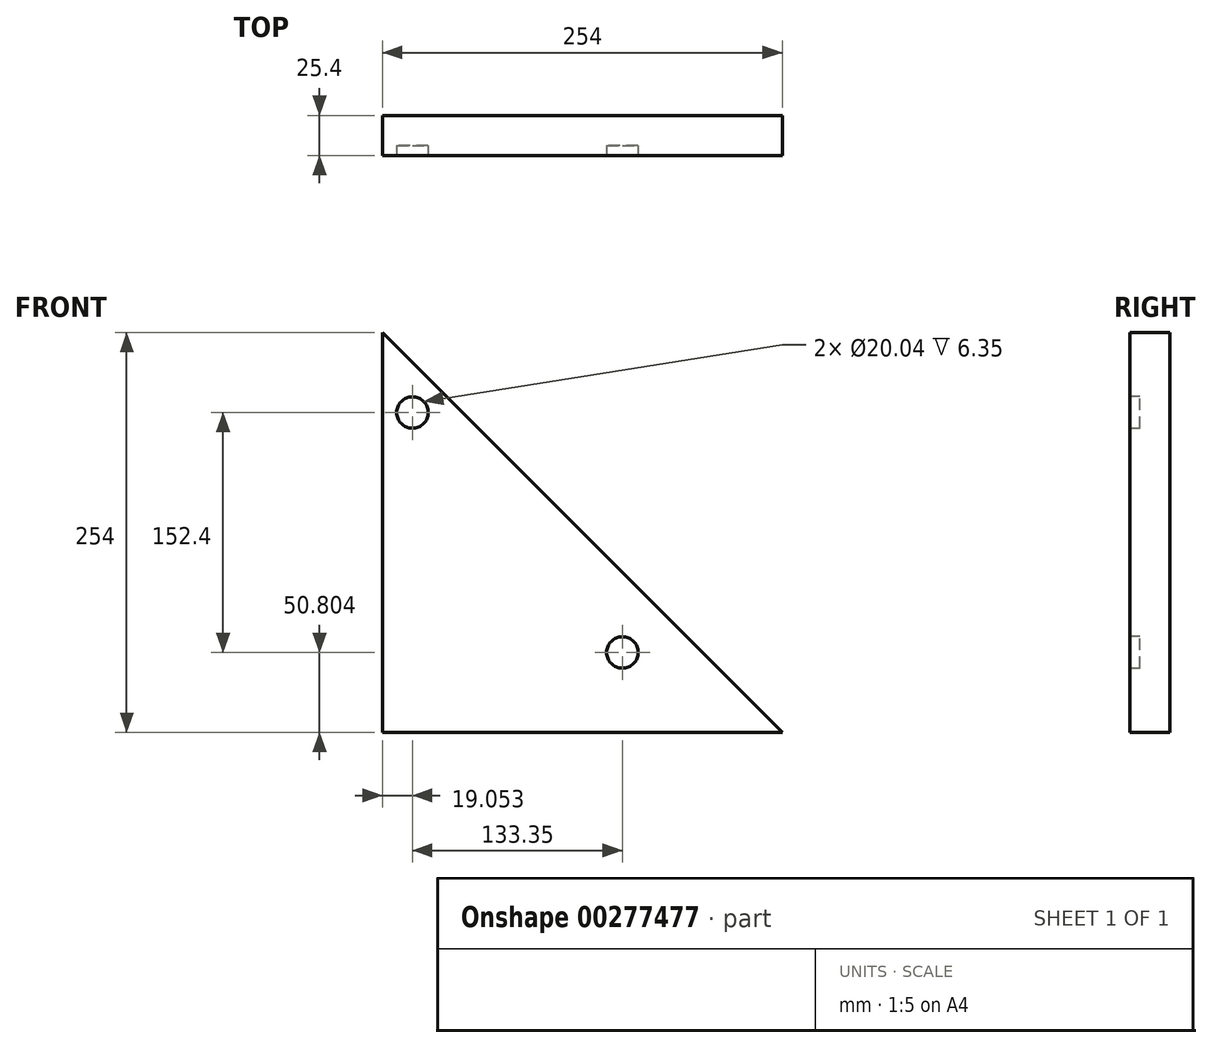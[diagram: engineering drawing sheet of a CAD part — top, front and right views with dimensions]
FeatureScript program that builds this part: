
annotation { "Feature Type Name" : "Feature", "Feature Type Description" : "" }
export const myFeature = defineFeature(function(context is Context, id is Id, definition is map)
    precondition{}
    {
        {
            var Q0;
            Q0=qCreatedBy(makeId("Front.planeOp"),FACE);
            var sketch = newSketch(context, id + "F0", { "sketchPlane" : qUnion([Q0])});
            skLineSegment(sketch, "E0.bottom", {"start": v(-41.24, 85.5) * mm, "end": v(212.76, 85.5) * mm});
            skLineSegment(sketch, "E0.top", {"start": v(-41.24, -168.5) * mm, "end": v(212.76, -168.5) * mm});
            skLineSegment(sketch, "E0.left", {"start": v(-41.24, 85.5) * mm, "end": v(-41.24, -168.5) * mm});
            skLineSegment(sketch, "E0.right", {"start": v(212.76, 85.5) * mm, "end": v(212.76, -168.5) * mm});
            skLineSegment(sketch, "E1", {"start": v(-41.24, 85.5) * mm, "end": v(212.76, -168.5) * mm});
            skSolve(sketch);
        }
        {
            var Q0;
            Q0=makeQuery(id+"F0.imprint","IMPRINT",FACE,{"disambiguationData":[TD([[makeQuery(id+"F0.imprint","IMPRINT",EDGE,{"derivedFrom":sQuery(id+"F0.wireOp",EDGE,"E0.top")}),1.0]])]});
            extrude(context, id + "F1", {"entities" : qUnion([Q0]), "depth" : 25.4 * mm});
        }
        {
            var Q0;
            Q0=makeQuery(id+"F1.opExtrude","CAP_FACE",FACE,{"disambiguationData":[OSD([sQuery(id+"F0.wireOp",EDGE,"E0.top"),sQuery(id+"F0.wireOp",EDGE,"E0.left"),sQuery(id+"F0.wireOp",EDGE,"E1")])],"isStart":false});
            var sketch = newSketch(context, id + "F2", { "sketchPlane" : qUnion([Q0])});
            skCircle(sketch, "E2", {"center": v(-22.19, 34.7) * mm, "radius": 10.02 * mm});
            skCircle(sketch, "E3", {"center": v(111.16, -117.7) * mm, "radius": 10.02 * mm});
            skSolve(sketch);
        }
        {
            var Q0;
            Q0 = qSketchRegion(id + "F2", true);
            extrude(context, id + "F3", {"entities" : qUnion([Q0]), "operationType" : NewBodyOperationType.REMOVE, "oppositeDirection" : true, "depth" : 6.35 * mm});
        }
    });
